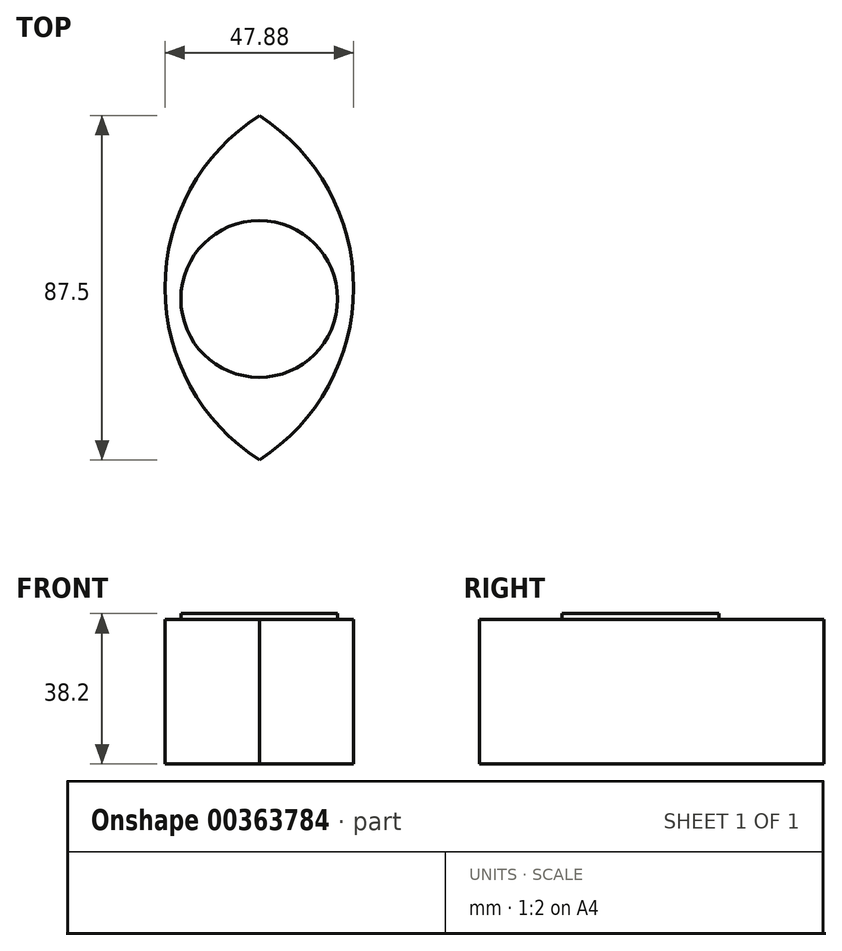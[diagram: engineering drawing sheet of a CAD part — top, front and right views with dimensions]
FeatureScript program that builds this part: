
annotation { "Feature Type Name" : "Feature", "Feature Type Description" : "" }
export const myFeature = defineFeature(function(context is Context, id is Id, definition is map)
    precondition{}
    {
        {
            var Q0;
            Q0=qCreatedBy(makeId("Top.planeOp"),FACE);
            var sketch = newSketch(context, id + "F0", { "sketchPlane" : qUnion([Q0])});
            skCircle(sketch, "E0", {"center": v(0, 0) * mm, "radius": 51.94 * mm});
            skSolve(sketch);
        }
        {
            var Q0;
            Q0 = qSketchRegion(id + "F0", true);
            extrude(context, id + "F1", {"entities" : qUnion([Q0]), "depth" : 109 * mm});
        }
        {
            var Q0;
            Q0=makeQuery(id+"F1.opExtrude","SWEPT_BODY",BODY,{"disambiguationData":[OSD([sQuery(id+"F0.wireOp",EDGE,"E0")])]});
            transform(context, id + "F2", {"entities" : qUnion([Q0]), "transformType" : TransformType.TRANSLATION_3D, "dx" : 56 * mm, "dy" : 0 * mm, "dz" : 72.3 * mm, "makeCopy" : true});
        }
        {
            var Q0;
            Q0=makeQuery(id+"F1.opExtrude","SWEPT_BODY",BODY,{"disambiguationData":[OSD([sQuery(id+"F0.wireOp",EDGE,"E0")])]});
            var Q1;
            Q1=makeQuery(id+"F2.opPattern","COPY",BODY,{"derivedFrom":makeQuery(id+"F1.opExtrude","SWEPT_BODY",BODY,{"disambiguationData":[OSD([sQuery(id+"F0.wireOp",EDGE,"E0")])]}),"instanceName":"1"});
            booleanBodies(context, id + "F3", {"operationType" : BooleanOperationType.INTERSECTION, "tools" : qUnion([Q0, Q1])});
        }
        {
            var Q0;
            Q0=makeQuery(id+"F1.opExtrude","CAP_FACE",FACE,{"disambiguationData":[OSD([sQuery(id+"F0.wireOp",EDGE,"E0")])],"isStart":false});
            var sketch = newSketch(context, id + "F4", { "sketchPlane" : qUnion([Q0])});
            skCircle(sketch, "E1", {"center": v(27.99, -2.83) * mm, "radius": 19.9 * mm});
            skSolve(sketch);
        }
        {
            var Q0;
            Q0 = qSketchRegion(id + "F4", true);
            extrude(context, id + "F5", {"entities" : qUnion([Q0]), "depth" : 1.5 * mm});
        }
    });
